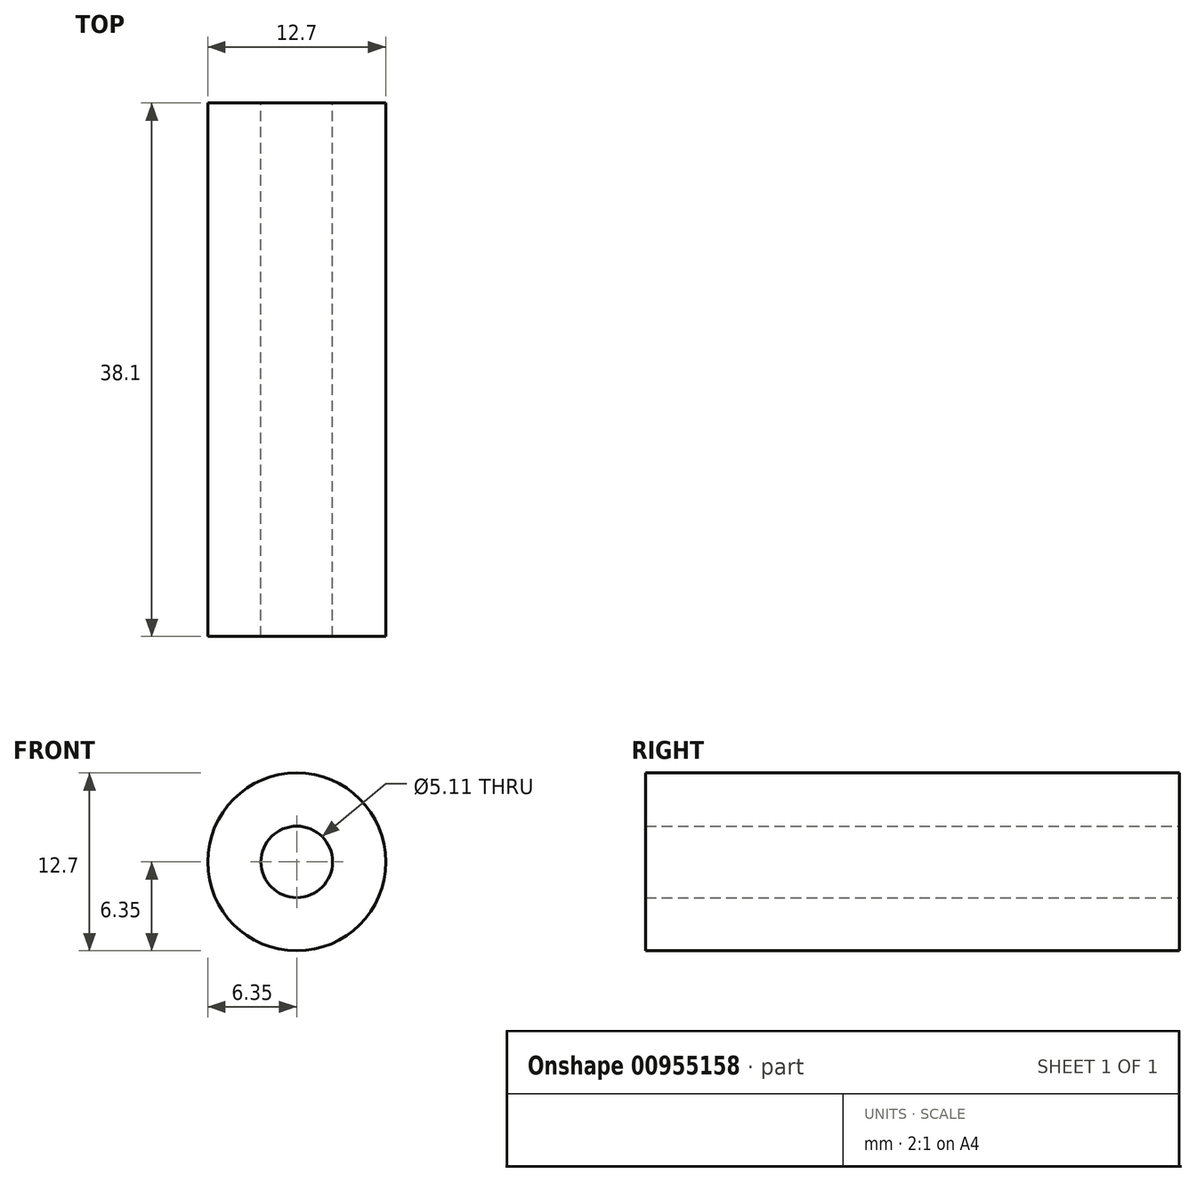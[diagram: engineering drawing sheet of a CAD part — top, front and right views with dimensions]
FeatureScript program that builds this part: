
annotation { "Feature Type Name" : "Feature", "Feature Type Description" : "" }
export const myFeature = defineFeature(function(context is Context, id is Id, definition is map)
    precondition{}
    {
        {
            var Q0;
            Q0=qCreatedBy(makeId("Front.planeOp"),FACE);
            var sketch = newSketch(context, id + "F0", { "sketchPlane" : qUnion([Q0])});
            skCircle(sketch, "E0", {"center": v(0, 0) * mm, "radius": 2.55 * mm});
            skCircle(sketch, "E1", {"center": v(0, 0) * mm, "radius": 6.35 * mm});
            skSolve(sketch);
        }
        {
            var Q0;
            Q0=qSketchRegion(id+"F0",true);
            extrude(context, id + "F1", {"entities" : qUnion([Q0]), "depth" : 38.1 * mm, "offsetDistance" : 25.4 * mm});
        }
    });
